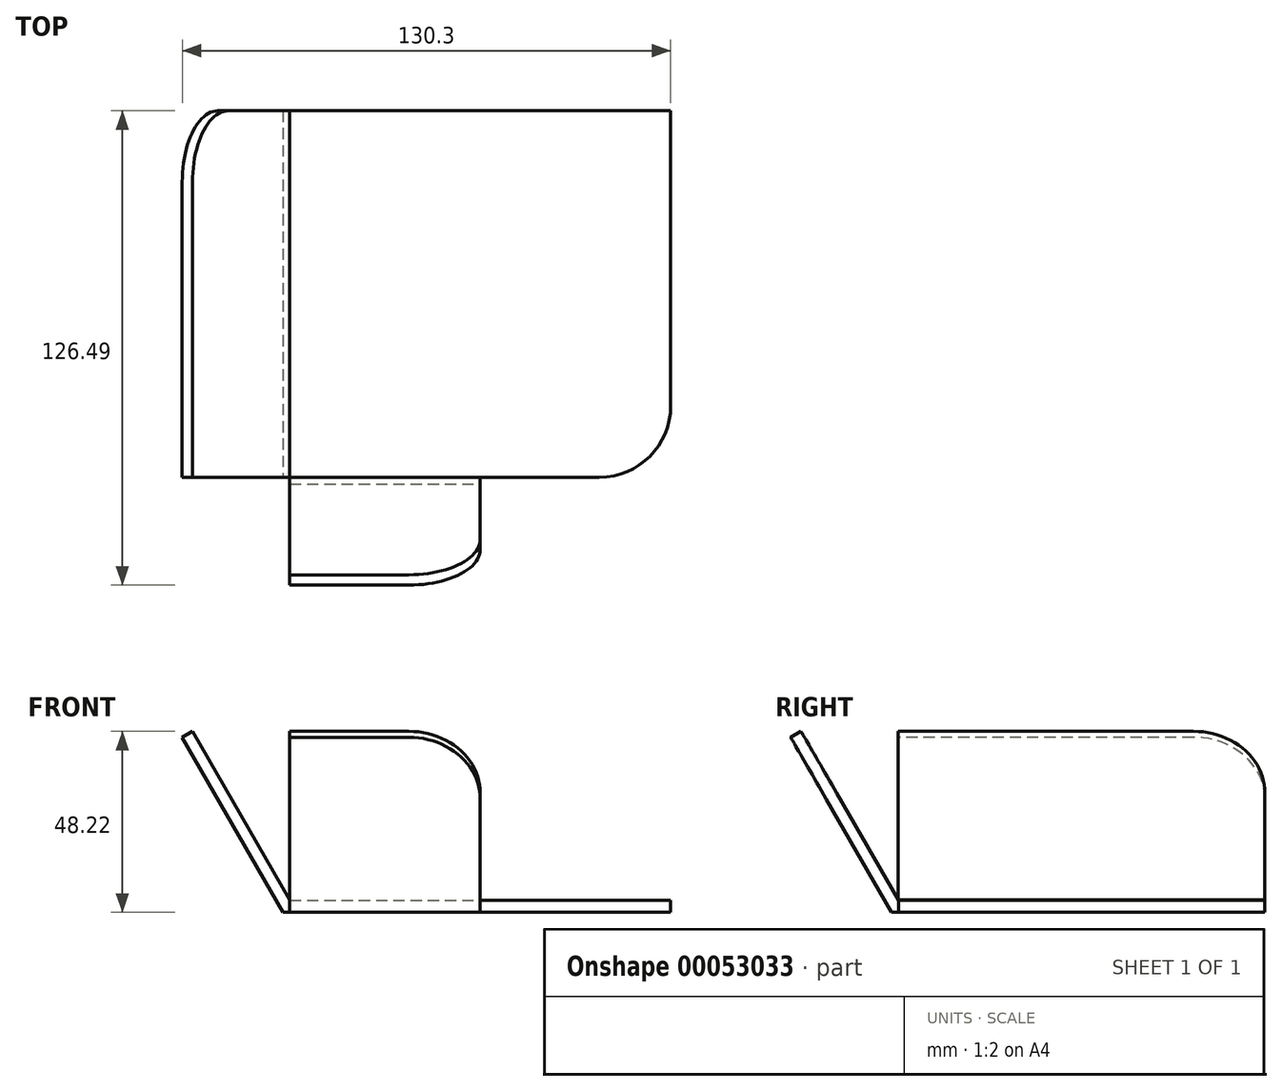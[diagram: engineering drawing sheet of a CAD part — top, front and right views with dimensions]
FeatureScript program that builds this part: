
annotation { "Feature Type Name" : "Feature", "Feature Type Description" : "" }
export const myFeature = defineFeature(function(context is Context, id is Id, definition is map)
    precondition{}
    {
        {
            var Q0;
            Q0=qCreatedBy(makeId("Top.planeOp"),FACE);
            var sketch = newSketch(context, id + "F0", { "sketchPlane" : qUnion([Q0])});
            skLineSegment(sketch, "E0.bottom", {"start": v(0, 0) * mm, "end": v(-152.4, 0) * mm});
            skLineSegment(sketch, "E0.top", {"start": v(0, 165.1) * mm, "end": v(-152.4, 165.1) * mm});
            skLineSegment(sketch, "E0.left", {"start": v(0, 0) * mm, "end": v(0, 165.1) * mm});
            skLineSegment(sketch, "E0.right", {"start": v(-152.4, 0) * mm, "end": v(-152.4, 165.1) * mm});
            skSolve(sketch);
        }
        {
            var Q0;
            Q0 = qSketchRegion(id + "F0", true);
            extrude(context, id + "F1", {"entities" : qUnion([Q0]), "depth" : 50.8 * mm});
        }
        {
            var Q0;
            Q0=makeQuery(id+"F1.opExtrude","SWEPT_FACE",FACE,{"disambiguationData":[OSD([sQuery(id+"F0.wireOp",EDGE,"E0.left")])]});
            var sketch = newSketch(context, id + "F2", { "sketchPlane" : qUnion([Q0])});
            skLineSegment(sketch, "E1", {"start": v(165.1, 0) * mm, "end": v(65.53, 0) * mm});
            skLineSegment(sketch, "E2", {"start": v(65.53, 0) * mm, "end": v(38.6, 46.63) * mm});
            skLineSegment(sketch, "E3", {"start": v(38.6, 46.63) * mm, "end": v(41.36, 48.22) * mm});
            skLineSegment(sketch, "E4", {"start": v(41.36, 48.22) * mm, "end": v(67.37, 3.17) * mm});
            skLineSegment(sketch, "E5", {"start": v(67.37, 3.17) * mm, "end": v(165.1, 3.17) * mm});
            skLineSegment(sketch, "E6", {"start": v(165.1, 3.17) * mm, "end": v(165.1, 0) * mm});
            skSolve(sketch);
        }
        {
            var Q0;
            {var subQ3=sQuery(id+"F2.wireOp",EDGE,"E2");Q0=makeQuery(id+"F2.imprint","IMPRINT",FACE,{"disambiguationData":[TD([[makeQuery(id+"F2.imprint","IMPRINT",EDGE,{"derivedFrom":subQ3}),1.0]])]});}
            extrude(context, id + "F3", {"entities" : qUnion([Q0]), "operationType" : NewBodyOperationType.REMOVE, "oppositeDirection" : true, "depth" : 101.6 * mm});
        }
        {
            var Q0;
            Q0=makeQuery(id+"F1.opExtrude","SWEPT_FACE",FACE,{"disambiguationData":[OSD([sQuery(id+"F0.wireOp",EDGE,"E0.bottom")])]});
            var sketch = newSketch(context, id + "F4", { "sketchPlane" : qUnion([Q0])});
            skLineSegment(sketch, "E7", {"start": v(0, 3.17) * mm, "end": v(0, 0) * mm});
            skLineSegment(sketch, "E8", {"start": v(0, 0) * mm, "end": v(-103.38, 0) * mm});
            skLineSegment(sketch, "E9", {"start": v(-103.38, 0) * mm, "end": v(-130.3, 46.63) * mm});
            skLineSegment(sketch, "E10", {"start": v(-130.3, 46.63) * mm, "end": v(-127.55, 48.22) * mm});
            skLineSegment(sketch, "E11", {"start": v(-127.55, 48.22) * mm, "end": v(-101.54, 3.17) * mm});
            skLineSegment(sketch, "E12", {"start": v(-101.54, 3.17) * mm, "end": v(0, 3.17) * mm});
            skSolve(sketch);
        }
        {
            var Q0;
            {var subQ7=sQuery(id+"F4.wireOp",EDGE,"E9");Q0=makeQuery(id+"F4.imprint","IMPRINT",FACE,{"disambiguationData":[TD([[makeQuery(id+"F4.imprint","IMPRINT",EDGE,{"derivedFrom":subQ7}),1.0]])]});}
            extrude(context, id + "F5", {"entities" : qUnion([Q0]), "operationType" : NewBodyOperationType.REMOVE, "endBound" : BoundingType.THROUGH_ALL, "oppositeDirection" : true, "depth" : 25.4 * mm});
        }
        {
            var Q0;
            Q0=makeQuery(id+"F5.boolean.opBoolean","COPY",FACE,{"derivedFrom":makeQuery(id+"F5.opExtrude","SWEPT_FACE",FACE,{"disambiguationData":[OSD([sQuery(id+"F4.wireOp",EDGE,"E11")])]})});
            var sketch = newSketch(context, id + "F6", { "sketchPlane" : qUnion([Q0])});
            skLineSegment(sketch, "E13.bottom", {"start": v(0, 105.54) * mm, "end": v(67.31, 105.54) * mm});
            skLineSegment(sketch, "E13.top", {"start": v(0, 53.63) * mm, "end": v(67.31, 53.63) * mm});
            skLineSegment(sketch, "E13.left", {"start": v(0, 105.54) * mm, "end": v(0, 53.63) * mm});
            skLineSegment(sketch, "E13.right", {"start": v(67.31, 105.54) * mm, "end": v(67.31, 53.63) * mm});
            skLineSegment(sketch, "E14", {"start": v(67.31, 105.54) * mm, "end": v(146.05, 105.54) * mm});
            skLineSegment(sketch, "E15", {"start": v(165.1, 86.49) * mm, "end": v(165.1, 53.63) * mm});
            skLineSegment(sketch, "E16", {"start": v(165.1, 53.63) * mm, "end": v(67.31, 53.63) * mm});
            skPoint(sketch, "E17.visualSharp", {"position": v(165.1, 105.54) * mm});
            skArc(sketch, "E17.filletArc", {"start": v(165.1, 86.49) * mm, "mid": v(159.52, 99.96) * mm, "end": v(146.05, 105.54) * mm});
            skSolve(sketch);
        }
        {
            var Q0;
            {var subQ0=sQuery(id+"F6.wireOp",EDGE,"E17.filletArc");Q0=makeQuery(id+"F6.imprint","IMPRINT",FACE,{"disambiguationData":[TD([[makeQuery(id+"F6.imprint","IMPRINT",EDGE,{"derivedFrom":subQ0}),-1.0]])]});}
            var Q1;
            Q1=makeQuery(id+"F6.imprint","IMPRINT",FACE,{"disambiguationData":[TD([[makeQuery(id+"F6.imprint","IMPRINT",EDGE,{"derivedFrom":sQuery(id+"F6.wireOp",EDGE,"E13.bottom")}),1.0]])]});
            extrude(context, id + "F7", {"entities" : qUnion([Q0, Q1]), "operationType" : NewBodyOperationType.REMOVE, "oppositeDirection" : true, "depth" : 25.4 * mm});
        }
        {
            var Q0;
            Q0=makeQuery(id+"F1.opExtrude","CAP_FACE",FACE,{"disambiguationData":[OSD([sQuery(id+"F0.wireOp",EDGE,"E0.bottom"),sQuery(id+"F0.wireOp",EDGE,"E0.top"),sQuery(id+"F0.wireOp",EDGE,"E0.left"),sQuery(id+"F0.wireOp",EDGE,"E0.right")])],"isStart":true});
            var sketch = newSketch(context, id + "F8", { "sketchPlane" : qUnion([Q0])});
            skLineSegment(sketch, "E18.bottom", {"start": v(-101.6, 0) * mm, "end": v(-108.91, 0) * mm});
            skLineSegment(sketch, "E18.top", {"start": v(-101.6, -67.31) * mm, "end": v(-108.91, -67.31) * mm});
            skLineSegment(sketch, "E18.left", {"start": v(-101.6, 0) * mm, "end": v(-101.6, -67.31) * mm});
            skLineSegment(sketch, "E18.right", {"start": v(-108.91, 0) * mm, "end": v(-108.91, -67.31) * mm});
            skSolve(sketch);
        }
        {
            var Q0;
            {var subQ3=sQuery(id+"F8.wireOp",EDGE,"E18.right");Q0=makeQuery(id+"F8.imprint","IMPRINT",FACE,{"disambiguationData":[TD([[makeQuery(id+"F8.imprint","IMPRINT",EDGE,{"derivedFrom":subQ3}),1.0]])]});}
            var Q1;
            {var subQ0=sQuery(id+"F8.wireOp",EDGE,"E18.left");var subQ4=sQuery(id+"F8.wireOp",EDGE,"E18.bottom");var subQ5=makeQuery(id+"F8.imprint","INTERSECT",VERTEX,{"derivedFrom":[subQ4,subQ0]});Q1=makeQuery(id+"F8.imprint","IMPRINT",FACE,{"disambiguationData":[TD([[makeQuery(id+"F8.imprint","IMPRINT",EDGE,{"disambiguationData":[TD([[subQ5,-1.0]])],"derivedFrom":subQ4}),1.0]])]});}
            extrude(context, id + "F9", {"entities" : qUnion([Q0, Q1]), "operationType" : NewBodyOperationType.REMOVE, "endBound" : BoundingType.THROUGH_ALL, "oppositeDirection" : true, "depth" : 25.4 * mm});
        }
        {
            var Q0;
            Q0=makeQuery(id+"F3.boolean.opBoolean","COPY",FACE,{"derivedFrom":makeQuery(id+"F3.opExtrude","SWEPT_FACE",FACE,{"disambiguationData":[OSD([sQuery(id+"F2.wireOp",EDGE,"E4")])]})});
            var sketch = newSketch(context, id + "F10", { "sketchPlane" : qUnion([Q0])});
            skLineSegment(sketch, "E19.bottom", {"start": v(101.6, 21.08) * mm, "end": v(69.85, 21.08) * mm});
            skLineSegment(sketch, "E19.top", {"start": v(101.6, -30.93) * mm, "end": v(50.8, -30.93) * mm});
            skLineSegment(sketch, "E19.left", {"start": v(101.6, 21.08) * mm, "end": v(101.6, -30.93) * mm});
            skLineSegment(sketch, "E19.right", {"start": v(50.8, 2.03) * mm, "end": v(50.8, -30.93) * mm});
            skPoint(sketch, "E20.visualSharp", {"position": v(50.8, 21.08) * mm});
            skArc(sketch, "E20.filletArc", {"start": v(69.85, 21.08) * mm, "mid": v(56.38, 15.5) * mm, "end": v(50.8, 2.03) * mm});
            skSolve(sketch);
        }
        {
            var Q0;
            {var subQ3=sQuery(id+"F10.wireOp",EDGE,"E19.right");Q0=makeQuery(id+"F10.imprint","IMPRINT",FACE,{"disambiguationData":[TD([[makeQuery(id+"F10.imprint","IMPRINT",EDGE,{"derivedFrom":subQ3}),-1.0]])]});}
            extrude(context, id + "F11", {"entities" : qUnion([Q0]), "operationType" : NewBodyOperationType.REMOVE, "oppositeDirection" : true, "depth" : 25.4 * mm});
        }
        {
            var Q0;
            Q0=makeQuery(id+"F3.boolean.opBoolean","COPY",FACE,{"derivedFrom":makeQuery(id+"F3.opExtrude","SWEPT_FACE",FACE,{"disambiguationData":[OSD([sQuery(id+"F2.wireOp",EDGE,"E5")])]})});
            var sketch = newSketch(context, id + "F12", { "sketchPlane" : qUnion([Q0])});
            skLineSegment(sketch, "E21.bottom", {"start": v(-101.6, 165.1) * mm, "end": v(0, 165.1) * mm});
            skLineSegment(sketch, "E21.top", {"start": v(-101.6, 67.37) * mm, "end": v(-19.05, 67.37) * mm});
            skLineSegment(sketch, "E21.left", {"start": v(-101.6, 165.1) * mm, "end": v(-101.6, 67.37) * mm});
            skLineSegment(sketch, "E21.right", {"start": v(0, 165.1) * mm, "end": v(0, 86.42) * mm});
            skPoint(sketch, "E22.visualSharp", {"position": v(0, 67.37) * mm});
            skArc(sketch, "E22.filletArc", {"start": v(-19.05, 67.37) * mm, "mid": v(-5.58, 72.94) * mm, "end": v(0, 86.42) * mm});
            skSolve(sketch);
        }
        {
            var Q0;
            {var subQ0=sQuery(id+"F12.wireOp",EDGE,"E22.filletArc");Q0=makeQuery(id+"F12.imprint","IMPRINT",FACE,{"disambiguationData":[TD([[makeQuery(id+"F12.imprint","IMPRINT",EDGE,{"derivedFrom":subQ0}),-1.0]])]});}
            extrude(context, id + "F13", {"entities" : qUnion([Q0]), "operationType" : NewBodyOperationType.REMOVE, "oppositeDirection" : true, "depth" : 25.4 * mm});
        }
        {
            var Q0;
            Q0=makeQuery(id+"F3.boolean.opBoolean","COPY",FACE,{"derivedFrom":makeQuery(id+"F3.opExtrude","SWEPT_FACE",FACE,{"disambiguationData":[OSD([sQuery(id+"F2.wireOp",EDGE,"E5")])]})});
            var sketch = newSketch(context, id + "F14", { "sketchPlane" : qUnion([Q0])});
            skLineSegment(sketch, "E23.bottom", {"start": v(-50.8, 67.37) * mm, "end": v(10.2, 67.37) * mm});
            skLineSegment(sketch, "E23.top", {"start": v(-50.8, 55.99) * mm, "end": v(10.2, 55.99) * mm});
            skLineSegment(sketch, "E23.left", {"start": v(-50.8, 67.37) * mm, "end": v(-50.8, 55.99) * mm});
            skLineSegment(sketch, "E23.right", {"start": v(10.2, 67.37) * mm, "end": v(10.2, 55.99) * mm});
            skSolve(sketch);
        }
        {
            var Q0;
            Q0 = qSketchRegion(id + "F14", true);
            extrude(context, id + "F15", {"entities" : qUnion([Q0]), "operationType" : NewBodyOperationType.REMOVE, "oppositeDirection" : true, "depth" : 50.8 * mm});
        }
    });
